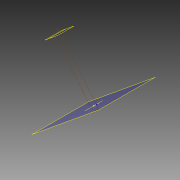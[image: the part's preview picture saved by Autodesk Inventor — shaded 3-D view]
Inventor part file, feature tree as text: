
AUTODESK INVENTOR PART (.ipt)
format: ipt  version: 2014 SP1 (Build 180222100, 222)  size: 299,008 bytes
history: native  units: mm (DEFAULTED — no unit token found)
features: other x78, extrude x75, sketch x3, plane x1, pattern_linear x1
ambient origin geometry x8: Origin, YZ Plane, XZ Plane, XY Plane, X Axis, Y Axis, Z Axis, Center Point
bodies: Body1 (feature_tree), Body2 (feature_tree), Body3 (feature_tree), Body4 (feature_tree), Body5 (feature_tree), Body6 (feature_tree), Body7 (feature_tree), Body8 (feature_tree), Body9 (feature_tree), Body10 (feature_tree), Body11 (feature_tree), Body12 (feature_tree), Body13 (feature_tree), Body14 (feature_tree), Body15 (feature_tree), Body16 (feature_tree), Body17 (feature_tree), Body18 (feature_tree), Body19 (feature_tree), Body20 (feature_tree), Body21 (feature_tree), Body22 (feature_tree), Body23 (feature_tree), Body24 (feature_tree), Body25 (feature_tree), Body26 (feature_tree), Body27 (feature_tree), Body28 (feature_tree), Body29 (feature_tree), Body30 (feature_tree), Body31 (feature_tree), Body32 (feature_tree), Body33 (feature_tree), Body34 (feature_tree), Body35 (feature_tree), Body36 (feature_tree), Body37 (feature_tree), Body38 (feature_tree), Body39 (feature_tree), Body40 (feature_tree), Body41 (feature_tree), Body42 (feature_tree), Body43 (feature_tree), Body44 (feature_tree), Body45 (feature_tree), Body46 (feature_tree), Body47 (feature_tree), Body48 (feature_tree), Body49 (feature_tree), Body50 (feature_tree), Body51 (feature_tree), Body52 (feature_tree), Body53 (feature_tree), Body54 (feature_tree), Body55 (feature_tree), Body56 (feature_tree), Body57 (feature_tree), Body58 (feature_tree), Body59 (feature_tree), Body60 (feature_tree), Body61 (feature_tree), Body62 (feature_tree), Body63 (feature_tree), Body64 (feature_tree), Body65 (feature_tree), Body66 (feature_tree), Body67 (feature_tree), Body68 (feature_tree), Body69 (feature_tree), Body70 (feature_tree), Body71 (feature_tree), Body72 (feature_tree), Body73 (feature_tree), Body74 (feature_tree), Body75 (feature_tree)
feature tree (158):
  sketch  "Sketch Path"  dims[d8=0.0mm d9=0.0mm d16=25.4mm d19=2.54mm d20=0.0mm d21=750.0mm]
  other  "Cross Section Plane"
  other  "Work Axis1"
  other  "Work Axis2"
  plane  "Work Plane3"
  sketch  "Sketch4"  dims[d0=0.0mm]
  pattern_linear  "Rectangular Pattern2"  Spacing1=2.54mm  [1 undecoded]
  sketch  "Sketch5"  dims[d7=0.0mm]
  other  "Srf74"
  other  "Srf75"
  other  "Srf76"
  other  "Srf77"
  other  "Srf78"
  other  "Srf79"
  other  "Srf80"
  other  "Srf81"
  other  "Srf82"
  other  "Srf83"
  other  "Srf84"
  other  "Srf85"
  other  "Srf86"
  other  "Srf87"
  other  "Srf88"
  other  "Srf89"
  other  "Srf90"
  other  "Srf91"
  other  "Srf92"
  other  "Srf93"
  other  "Srf94"
  other  "Srf95"
  other  "Srf96"
  other  "Srf97"
  other  "Srf98"
  other  "Srf99"
  other  "Srf100"
  other  "Srf101"
  other  "Srf102"
  other  "Srf103"
  other  "Srf104"
  other  "Srf105"
  other  "Srf106"
  other  "Srf107"
  other  "Srf108"
  other  "Srf109"
  other  "Srf110"
  other  "Srf111"
  other  "Srf112"
  other  "Srf113"
  other  "Srf114"
  other  "Srf115"
  other  "Srf116"
  other  "Srf117"
  other  "Srf118"
  other  "Srf119"
  other  "Srf120"
  other  "Srf121"
  other  "Srf122"
  other  "Srf123"
  other  "Srf124"
  other  "Srf125"
  other  "Srf126"
  other  "Srf127"
  other  "Srf128"
  other  "Srf129"
  other  "Srf130"
  other  "Srf131"
  other  "Srf132"
  other  "Srf133"
  other  "Srf134"
  other  "Srf135"
  other  "Srf136"
  other  "Srf137"
  other  "Srf138"
  other  "Srf169"
  other  "Srf170"
  other  "Srf171"
  other  "Srf172"
  other  "Srf173"
  other  "Srf174"
  other  "Srf175"
  other  "Srf176"
  other  "Srf177"
  other  "Srf178"
  extrude  "ExtrusionSrf74"  Depth=750.0mm
  extrude  "ExtrusionSrf75"  [1 undecoded]
  extrude  "ExtrusionSrf76"  [1 undecoded]
  extrude  "ExtrusionSrf77"  [1 undecoded]
  extrude  "ExtrusionSrf78"  [1 undecoded]
  extrude  "ExtrusionSrf79"  [1 undecoded]
  extrude  "ExtrusionSrf80"  [1 undecoded]
  extrude  "ExtrusionSrf81"  [1 undecoded]
  extrude  "ExtrusionSrf82"  [1 undecoded]
  extrude  "ExtrusionSrf83"  [1 undecoded]
  extrude  "ExtrusionSrf84"  [1 undecoded]
  extrude  "ExtrusionSrf85"  [1 undecoded]
  extrude  "ExtrusionSrf86"  [1 undecoded]
  extrude  "ExtrusionSrf87"  [1 undecoded]
  extrude  "ExtrusionSrf88"  [1 undecoded]
  extrude  "ExtrusionSrf89"  [1 undecoded]
  extrude  "ExtrusionSrf90"  [1 undecoded]
  extrude  "ExtrusionSrf91"  [1 undecoded]
  extrude  "ExtrusionSrf92"  [1 undecoded]
  extrude  "ExtrusionSrf93"  [1 undecoded]
  extrude  "ExtrusionSrf94"  [1 undecoded]
  extrude  "ExtrusionSrf95"  [1 undecoded]
  extrude  "ExtrusionSrf96"  [1 undecoded]
  extrude  "ExtrusionSrf97"  [1 undecoded]
  extrude  "ExtrusionSrf98"  [1 undecoded]
  extrude  "ExtrusionSrf99"  [1 undecoded]
  extrude  "ExtrusionSrf100"  [1 undecoded]
  extrude  "ExtrusionSrf101"  [1 undecoded]
  extrude  "ExtrusionSrf102"  [1 undecoded]
  extrude  "ExtrusionSrf103"  [1 undecoded]
  extrude  "ExtrusionSrf104"  [1 undecoded]
  extrude  "ExtrusionSrf105"  [1 undecoded]
  extrude  "ExtrusionSrf106"  [1 undecoded]
  extrude  "ExtrusionSrf107"  [1 undecoded]
  extrude  "ExtrusionSrf108"  [1 undecoded]
  extrude  "ExtrusionSrf109"  [1 undecoded]
  extrude  "ExtrusionSrf110"  [1 undecoded]
  extrude  "ExtrusionSrf111"  [1 undecoded]
  extrude  "ExtrusionSrf112"  [1 undecoded]
  extrude  "ExtrusionSrf113"  [1 undecoded]
  extrude  "ExtrusionSrf114"  [1 undecoded]
  extrude  "ExtrusionSrf115"  [1 undecoded]
  extrude  "ExtrusionSrf116"  [1 undecoded]
  extrude  "ExtrusionSrf117"  [1 undecoded]
  extrude  "ExtrusionSrf118"  [1 undecoded]
  extrude  "ExtrusionSrf119"  [1 undecoded]
  extrude  "ExtrusionSrf120"  [1 undecoded]
  extrude  "ExtrusionSrf121"  [1 undecoded]
  extrude  "ExtrusionSrf122"  [1 undecoded]
  extrude  "ExtrusionSrf123"  [1 undecoded]
  extrude  "ExtrusionSrf124"  [1 undecoded]
  extrude  "ExtrusionSrf125"  [1 undecoded]
  extrude  "ExtrusionSrf126"  [1 undecoded]
  extrude  "ExtrusionSrf127"  [1 undecoded]
  extrude  "ExtrusionSrf128"  [1 undecoded]
  extrude  "ExtrusionSrf129"  [1 undecoded]
  extrude  "ExtrusionSrf130"  [1 undecoded]
  extrude  "ExtrusionSrf131"  [1 undecoded]
  extrude  "ExtrusionSrf132"  [1 undecoded]
  extrude  "ExtrusionSrf133"  [1 undecoded]
  extrude  "ExtrusionSrf134"  [1 undecoded]
  extrude  "ExtrusionSrf135"  [1 undecoded]
  extrude  "ExtrusionSrf136"  [1 undecoded]
  extrude  "ExtrusionSrf137"  [1 undecoded]
  extrude  "ExtrusionSrf138"  [1 undecoded]
  extrude  "ExtrusionSrf169"  [1 undecoded]
  extrude  "ExtrusionSrf170"  [1 undecoded]
  extrude  "ExtrusionSrf171"  [1 undecoded]
  extrude  "ExtrusionSrf172"  [1 undecoded]
  extrude  "ExtrusionSrf173"  [1 undecoded]
  extrude  "ExtrusionSrf174"  [1 undecoded]
  extrude  "ExtrusionSrf175"  [1 undecoded]
  extrude  "ExtrusionSrf176"  [1 undecoded]
  extrude  "ExtrusionSrf177"  [1 undecoded]
  extrude  "ExtrusionSrf178"  [1 undecoded]
note: 75 required parameter values undecoded (feature->parameter linkage not recoverable at this tier; creation-order binding heuristic only, values carry confidence <= 0.55)
